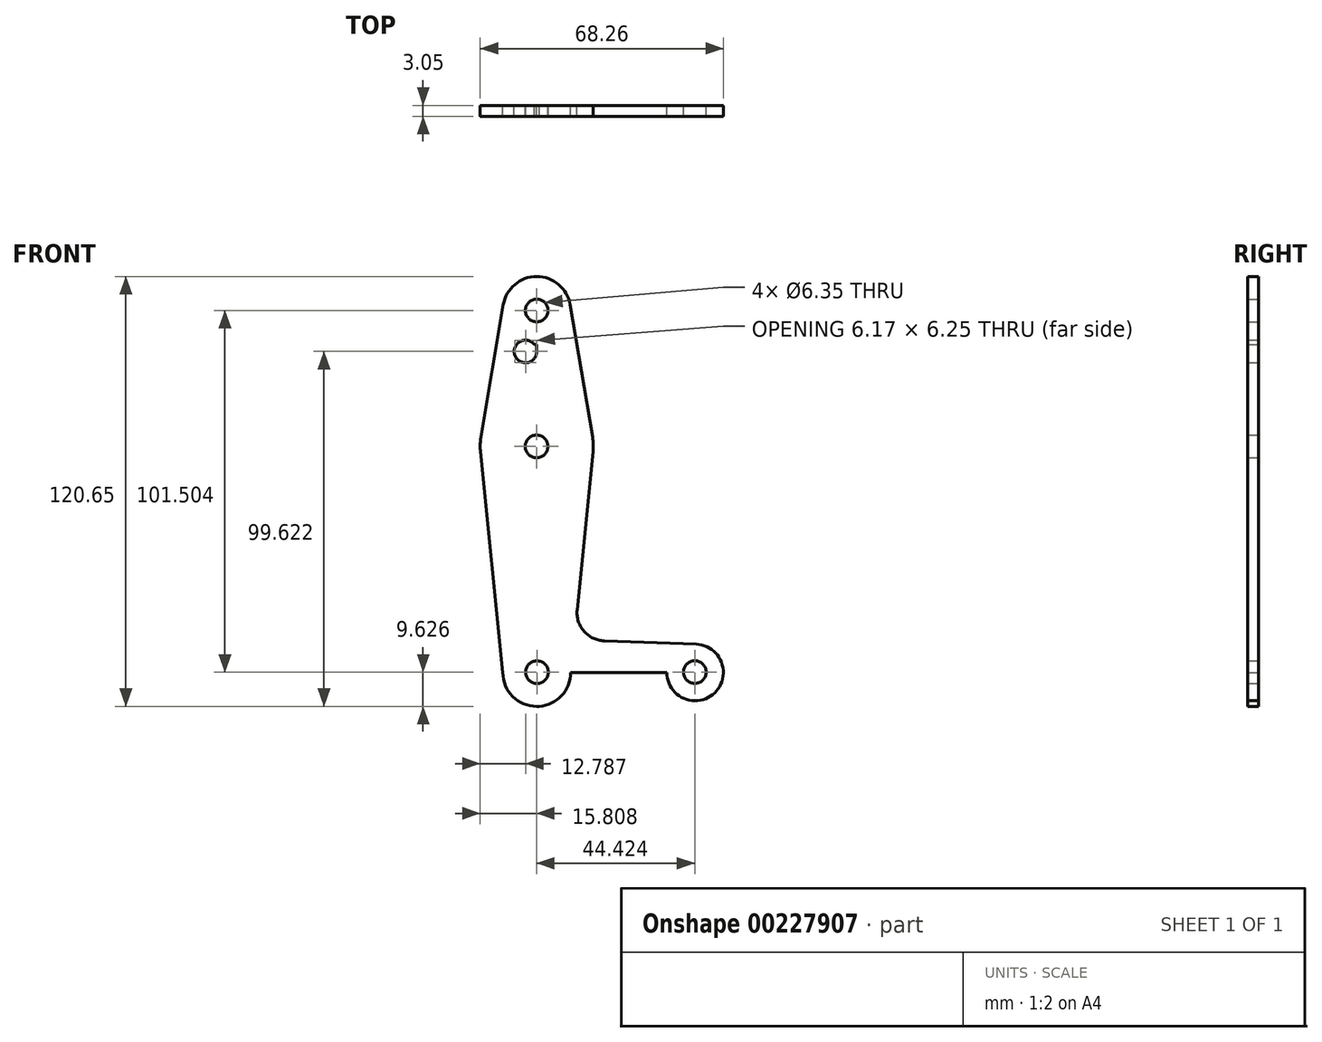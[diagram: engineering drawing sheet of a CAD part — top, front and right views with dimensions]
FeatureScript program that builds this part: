
annotation { "Feature Type Name" : "Feature", "Feature Type Description" : "" }
export const myFeature = defineFeature(function(context is Context, id is Id, definition is map)
    precondition{}
    {
        {
            var Q0;
            Q0=qCreatedBy(makeId("Front.planeOp"),FACE);
            var sketch = newSketch(context, id + "F0", { "sketchPlane" : qUnion([Q0])});
            skCircle(sketch, "E0", {"center": v(0, 0) * mm, "radius": 9.53 * mm});
            skCircle(sketch, "E1", {"center": v(0, 63.5) * mm, "radius": 15.88 * mm});
            skCircle(sketch, "E2", {"center": v(0, 101.6) * mm, "radius": 9.53 * mm});
            skCircle(sketch, "E3", {"center": v(44.45, 0) * mm, "radius": 7.94 * mm});
            skLineSegment(sketch, "E4", {"start": v(-9.4, 103.19) * mm, "end": v(-15.65, 66.15) * mm});
            skLineSegment(sketch, "E5", {"start": v(9.4, 103.19) * mm, "end": v(15.65, 66.15) * mm});
            skLineSegment(sketch, "E6", {"start": v(15.8, 61.91) * mm, "end": v(11.34, 17.6) * mm});
            skLineSegment(sketch, "E7", {"start": v(44.73, 7.93) * mm, "end": v(18.97, 8.85) * mm});
            skLineSegment(sketch, "E8", {"start": v(0, -9.53) * mm, "end": v(44.73, -7.93) * mm});
            skLineSegment(sketch, "E9", {"start": v(0, 101.6) * mm, "end": v(0, 0) * mm});
            skLineSegment(sketch, "E10", {"start": v(0, 0) * mm, "end": v(44.45, 0) * mm});
            skPoint(sketch, "E11.newPointB", {"position": v(0, 9.53) * mm});
            skArc(sketch, "E11.filletArc", {"start": v(11.34, 17.6) * mm, "mid": v(13.26, 11.57) * mm, "end": v(18.97, 8.85) * mm});
            skCircle(sketch, "E12", {"center": v(0, 101.6) * mm, "radius": 3.18 * mm});
            skCircle(sketch, "E13", {"center": v(-0.06, 63.44) * mm, "radius": 3.18 * mm});
            skCircle(sketch, "E14", {"center": v(0.06, 0.1) * mm, "radius": 3.18 * mm});
            skCircle(sketch, "E15", {"center": v(44.36, 0.11) * mm, "radius": 3.18 * mm});
            skCircle(sketch, "E16", {"center": v(-3.17, 90.1) * mm, "radius": 3.18 * mm});
            skLineSegment(sketch, "E17", {"start": v(-9.52, 0) * mm, "end": v(-15.8, 61.9) * mm});
            skSolve(sketch);
        }
        {
            var Q0;
            {var subQ0=sQuery(id+"F0.wireOp",EDGE,"E17");Q0=makeQuery(id+"F0.imprint","IMPRINT",FACE,{"disambiguationData":[TD([[makeQuery(id+"F0.imprint","IMPRINT",EDGE,{"derivedFrom":subQ0}),-1.0]])]});}
            var Q1;
            {var subQ0=sQuery(id+"F0.wireOp",EDGE,"E6");Q1=makeQuery(id+"F0.imprint","IMPRINT",FACE,{"disambiguationData":[TD([[makeQuery(id+"F0.imprint","IMPRINT",EDGE,{"derivedFrom":subQ0}),-1.0]])]});}
            var Q2;
            {var subQ1=sQuery(id+"F0.wireOp",EDGE,"E1");var subQ5=makeQuery(id+"F0.imprint","INTERSECT",VERTEX,{"derivedFrom":[subQ1,sQuery(id+"F0.wireOp",EDGE,"E5")]});Q2=makeQuery(id+"F0.imprint","IMPRINT",FACE,{"disambiguationData":[TD([[makeQuery(id+"F0.imprint","IMPRINT",EDGE,{"disambiguationData":[TD([[subQ5,-1.0]])],"derivedFrom":subQ1}),1.0]])]});}
            var Q3;
            {var subQ0=sQuery(id+"F0.wireOp",EDGE,"E5");Q3=makeQuery(id+"F0.imprint","IMPRINT",FACE,{"disambiguationData":[TD([[makeQuery(id+"F0.imprint","IMPRINT",EDGE,{"derivedFrom":subQ0}),-1.0]])]});}
            var Q4;
            {var subQ5=sQuery(id+"F0.wireOp",EDGE,"E4");Q4=makeQuery(id+"F0.imprint","IMPRINT",FACE,{"disambiguationData":[TD([[makeQuery(id+"F0.imprint","IMPRINT",EDGE,{"derivedFrom":subQ5}),1.0]])]});}
            var Q5;
            {var subQ0=sQuery(id+"F0.wireOp",EDGE,"E9");var subQ1=sQuery(id+"F0.wireOp",EDGE,"E0");var subQ2=makeQuery(id+"F0.imprint","INTERSECT",VERTEX,{"derivedFrom":[subQ1,subQ0]});Q5=makeQuery(id+"F0.imprint","IMPRINT",FACE,{"disambiguationData":[TD([[makeQuery(id+"F0.imprint","IMPRINT",EDGE,{"disambiguationData":[TD([[subQ2,1.0]])],"derivedFrom":subQ1}),1.0]])]});}
            var Q6;
            {var subQ1=sQuery(id+"F0.wireOp",EDGE,"E0");var subQ4=makeQuery(id+"F0.imprint","INTERSECT",VERTEX,{"derivedFrom":[subQ1,sQuery(id+"F0.wireOp",EDGE,"E17")]});Q6=makeQuery(id+"F0.imprint","IMPRINT",FACE,{"disambiguationData":[TD([[makeQuery(id+"F0.imprint","IMPRINT",EDGE,{"disambiguationData":[TD([[subQ4,1.0]])],"derivedFrom":subQ1}),1.0]])]});}
            var Q7;
            Q7=makeQuery(id+"F0.imprint","IMPRINT",FACE,{"disambiguationData":[TD([[makeQuery(id+"F0.imprint","IMPRINT",EDGE,{"derivedFrom":sQuery(id+"F0.wireOp",EDGE,"E12")}),-1.0]])]});
            var Q8;
            {var subQ0=sQuery(id+"F0.wireOp",EDGE,"E8");var subQ1=sQuery(id+"F0.wireOp",EDGE,"E0");var subQ2=makeQuery(id+"F0.imprint","INTERSECT",VERTEX,{"disambiguationData":[OD(1.0)],"derivedFrom":[subQ1,subQ0]});Q8=makeQuery(id+"F0.imprint","IMPRINT",FACE,{"disambiguationData":[TD([[makeQuery(id+"F0.imprint","IMPRINT",EDGE,{"disambiguationData":[TD([[subQ2,-1.0]])],"derivedFrom":subQ1}),-1.0]])]});}
            var Q9;
            Q9=makeQuery(id+"F0.imprint","IMPRINT",FACE,{"disambiguationData":[TD([[makeQuery(id+"F0.imprint","IMPRINT",EDGE,{"derivedFrom":sQuery(id+"F0.wireOp",EDGE,"E15")}),-1.0]])]});
            var Q10;
            {var subQ1=sQuery(id+"F0.wireOp",EDGE,"E1");var subQ5=makeQuery(id+"F0.imprint","INTERSECT",VERTEX,{"derivedFrom":[subQ1,sQuery(id+"F0.wireOp",EDGE,"E4")]});Q10=makeQuery(id+"F0.imprint","IMPRINT",FACE,{"disambiguationData":[TD([[makeQuery(id+"F0.imprint","IMPRINT",EDGE,{"disambiguationData":[TD([[subQ5,1.0]])],"derivedFrom":subQ1}),1.0]])]});}
            extrude(context, id + "F1", {"entities" : qUnion([Q0, Q1, Q2, Q3, Q4, Q5, Q6, Q7, Q8, Q9, Q10]), "depth" : 3.05 * mm});
        }
    });
